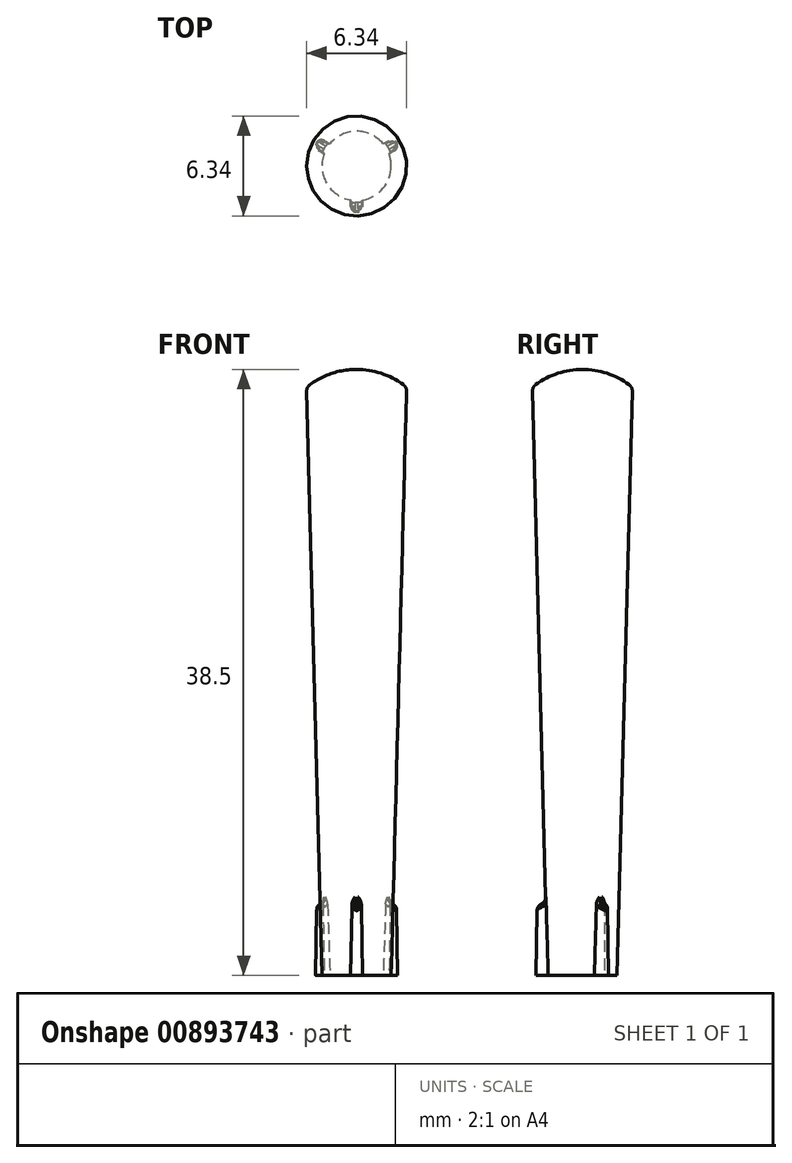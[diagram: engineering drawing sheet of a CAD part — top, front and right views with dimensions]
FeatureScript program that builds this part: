
annotation { "Feature Type Name" : "Feature", "Feature Type Description" : "" }
export const myFeature = defineFeature(function(context is Context, id is Id, definition is map)
    precondition{}
    {
        {
            var Q0;
            Q0=qCreatedBy(makeId("Front.planeOp"),FACE);
            var sketch = newSketch(context, id + "F0", { "sketchPlane" : qUnion([Q0])});
            skLineSegment(sketch, "E0", {"start": v(-2.2, 0) * mm, "end": v(-3.18, 37.36) * mm});
            skArc(sketch, "E1", {"start": v(-3.18, 37.36) * mm, "mid": v(-1.69, 38.2) * mm, "end": v(0, 38.5) * mm});
            skLineSegment(sketch, "E2", {"start": v(-2.2, 0) * mm, "end": v(0, 0) * mm});
            skLineSegment(sketch, "E3", {"start": v(0, 0) * mm, "end": v(0, 38.5) * mm});
            skSolve(sketch);
        }
        {
            var Q0;
            Q0=makeQuery(id+"F0.imprint","IMPRINT",FACE,{"disambiguationData":[TD([[makeQuery(id+"F0.imprint","IMPRINT",EDGE,{"derivedFrom":sQuery(id+"F0.wireOp",EDGE,"E0")}),-1.0]])]});
            var Q1;
            Q1=sQuery(id+"F0.wireOp",EDGE,"E3");
            revolve(context, id + "F1", {"surfaceOperationType" : NewSurfaceOperationType.NEW, "entities" : qUnion([Q0]), "axis" : qUnion([Q1]), "revolveType" : RevolveType.FULL});
        }
        {
            var Q0;
            Q0=makeQuery(id+"F1.opRevolve","SWEPT_EDGE",EDGE,{"disambiguationData":[OSD([sQuery(id+"F0.wireOp",EDGE,"E0"),sQuery(id+"F0.wireOp",EDGE,"E1")])]});
            fillet(context, id + "F2", {"entities" : qUnion([Q0]), "radius" : 0.5 * mm, "tangentPropagation" : true, "allowEdgeOverflow" : false});
        }
        {
            var Q0;
            Q0=makeQuery(id+"F1.opRevolve","SWEPT_FACE",FACE,{"disambiguationData":[OSD([sQuery(id+"F0.wireOp",EDGE,"E2")])]});
            var sketch = newSketch(context, id + "F3", { "sketchPlane" : qUnion([Q0])});
            skCircle(sketch, "E4", {"center": v(0, 2.58) * mm, "radius": 0.38 * mm});
            skLineSegment(sketch, "E5.bottom", {"start": v(0.37, 2.58) * mm, "end": v(-0.37, 2.58) * mm});
            skLineSegment(sketch, "E5.top", {"start": v(0.37, 2.17) * mm, "end": v(-0.37, 2.17) * mm});
            skLineSegment(sketch, "E5.left", {"start": v(0.37, 2.58) * mm, "end": v(0.37, 2.17) * mm});
            skLineSegment(sketch, "E5.right", {"start": v(-0.37, 2.58) * mm, "end": v(-0.37, 2.17) * mm});
            skPoint(sketch, "E5.middle", {"position": v(0, 2.37) * mm});
            skCircle(sketch, "E6.1.0", {"center": v(-2.23, -1.29) * mm, "radius": 0.38 * mm});
            skLineSegment(sketch, "E6.1.1", {"start": v(-2.42, -0.96) * mm, "end": v(-2.06, -0.76) * mm});
            skLineSegment(sketch, "E6.1.2", {"start": v(-2.06, -0.76) * mm, "end": v(-1.69, -1.4) * mm});
            skLineSegment(sketch, "E6.1.3", {"start": v(-2.04, -1.61) * mm, "end": v(-1.69, -1.4) * mm});
            skCircle(sketch, "E6.2.0", {"center": v(2.23, -1.29) * mm, "radius": 0.38 * mm});
            skLineSegment(sketch, "E6.2.1", {"start": v(2.04, -1.61) * mm, "end": v(1.69, -1.4) * mm});
            skLineSegment(sketch, "E6.2.2", {"start": v(1.69, -1.4) * mm, "end": v(2.06, -0.76) * mm});
            skLineSegment(sketch, "E6.2.3", {"start": v(2.42, -0.96) * mm, "end": v(2.06, -0.76) * mm});
            skPoint(sketch, "E6.center", {"position": v(0, 0) * mm});
            skSolve(sketch);
        }
        {
            var Q0;
            Q0 = qSketchRegion(id + "F3", true);
            extrude(context, id + "F4", {"entities" : qUnion([Q0]), "operationType" : NewBodyOperationType.ADD, "oppositeDirection" : true, "depth" : 5 * mm, "offsetDistance" : 25 * mm, "hasDraft" : true, "draftAngle" : 1 * degree, "draftPullDirection" : true});
        }
        {
            var Q0;
            Q0=qCreatedBy(makeId("Right.planeOp"),FACE);
            var sketch = newSketch(context, id + "F5", { "sketchPlane" : qUnion([Q0])});
            skLineSegment(sketch, "E7", {"start": v(-2.2, 0) * mm, "end": v(-3.21, 38.72) * mm, "construction": true});
            skArc(sketch, "E8", {"start": v(-2.6, 4.54) * mm, "mid": v(-2.4, 4.73) * mm, "end": v(-2.33, 5) * mm});
            skArc(sketch, "E9", {"start": v(-2.6, 4.54) * mm, "mid": v(-2.8, 4.36) * mm, "end": v(-2.88, 4.1) * mm});
            skLineSegment(sketch, "E10", {"start": v(-2.95, 0) * mm, "end": v(-2.86, 5) * mm, "construction": true});
            skLineSegment(sketch, "E11", {"start": v(-2.33, 5) * mm, "end": v(-2.86, 5) * mm});
            skLineSegment(sketch, "E12", {"start": v(-2.88, 4.1) * mm, "end": v(-2.86, 5) * mm});
            skLineSegment(sketch, "E13", {"start": v(0, 0) * mm, "end": v(0, 5) * mm, "construction": true});
            skSolve(sketch);
        }
        {
            var Q0;
            Q0 = qSketchRegion(id + "F5", true);
            var Q1;
            Q1=sQuery(id+"F5.wireOp",EDGE,"E13");
            revolve(context, id + "F6", {"operationType" : NewBodyOperationType.REMOVE, "surfaceOperationType" : NewSurfaceOperationType.NEW, "entities" : qUnion([Q0]), "axis" : qUnion([Q1]), "revolveType" : RevolveType.FULL, "oppositeDirection" : true});
        }
        {
            var Q0;
            Q0=makeQuery(id+"F6.boolean.opBoolean","INTERSECT",EDGE,{"derivedFrom":[makeQuery(id+"F4.opExtrude","SWEPT_FACE",FACE,{"disambiguationData":[OSD([sQuery(id+"F3.wireOp",EDGE,"E6.2.3")])]}),makeQuery(id+"F6.opRevolve","SWEPT_FACE",FACE,{"disambiguationData":[OSD([sQuery(id+"F5.wireOp",EDGE,"E8")])]})]});
            var Q1;
            Q1=makeQuery(id+"F6.boolean.opBoolean","INTERSECT",EDGE,{"derivedFrom":[makeQuery(id+"F4.opExtrude","SWEPT_FACE",FACE,{"disambiguationData":[OSD([sQuery(id+"F3.wireOp",EDGE,"E6.2.1")])]}),makeQuery(id+"F6.opRevolve","SWEPT_FACE",FACE,{"disambiguationData":[OSD([sQuery(id+"F5.wireOp",EDGE,"E8")])]})]});
            var Q2;
            Q2=makeQuery(id+"F6.boolean.opBoolean","INTERSECT",EDGE,{"derivedFrom":[makeQuery(id+"F4.opExtrude","SWEPT_FACE",FACE,{"disambiguationData":[OSD([sQuery(id+"F3.wireOp",EDGE,"E5.left")])]}),makeQuery(id+"F6.opRevolve","SWEPT_FACE",FACE,{"disambiguationData":[OSD([sQuery(id+"F5.wireOp",EDGE,"E8")])]})]});
            var Q3;
            Q3=makeQuery(id+"F6.boolean.opBoolean","INTERSECT",EDGE,{"derivedFrom":[makeQuery(id+"F4.opExtrude","SWEPT_FACE",FACE,{"disambiguationData":[OSD([sQuery(id+"F3.wireOp",EDGE,"E5.right")])]}),makeQuery(id+"F6.opRevolve","SWEPT_FACE",FACE,{"disambiguationData":[OSD([sQuery(id+"F5.wireOp",EDGE,"E8")])]})]});
            var Q4;
            Q4=makeQuery(id+"F6.boolean.opBoolean","INTERSECT",EDGE,{"derivedFrom":[makeQuery(id+"F4.opExtrude","SWEPT_FACE",FACE,{"disambiguationData":[OSD([sQuery(id+"F3.wireOp",EDGE,"E6.1.1")])]}),makeQuery(id+"F6.opRevolve","SWEPT_FACE",FACE,{"disambiguationData":[OSD([sQuery(id+"F5.wireOp",EDGE,"E8")])]})]});
            var Q5;
            Q5=makeQuery(id+"F6.boolean.opBoolean","INTERSECT",EDGE,{"derivedFrom":[makeQuery(id+"F4.opExtrude","SWEPT_FACE",FACE,{"disambiguationData":[OSD([sQuery(id+"F3.wireOp",EDGE,"E6.1.3")])]}),makeQuery(id+"F6.opRevolve","SWEPT_FACE",FACE,{"disambiguationData":[OSD([sQuery(id+"F5.wireOp",EDGE,"E8")])]})]});
            fillet(context, id + "F7", {"entities" : qUnion([Q0, Q1, Q2, Q3, Q4, Q5]), "radius" : 0.2 * mm, "tangentPropagation" : true, "allowEdgeOverflow" : false});
        }
    });
